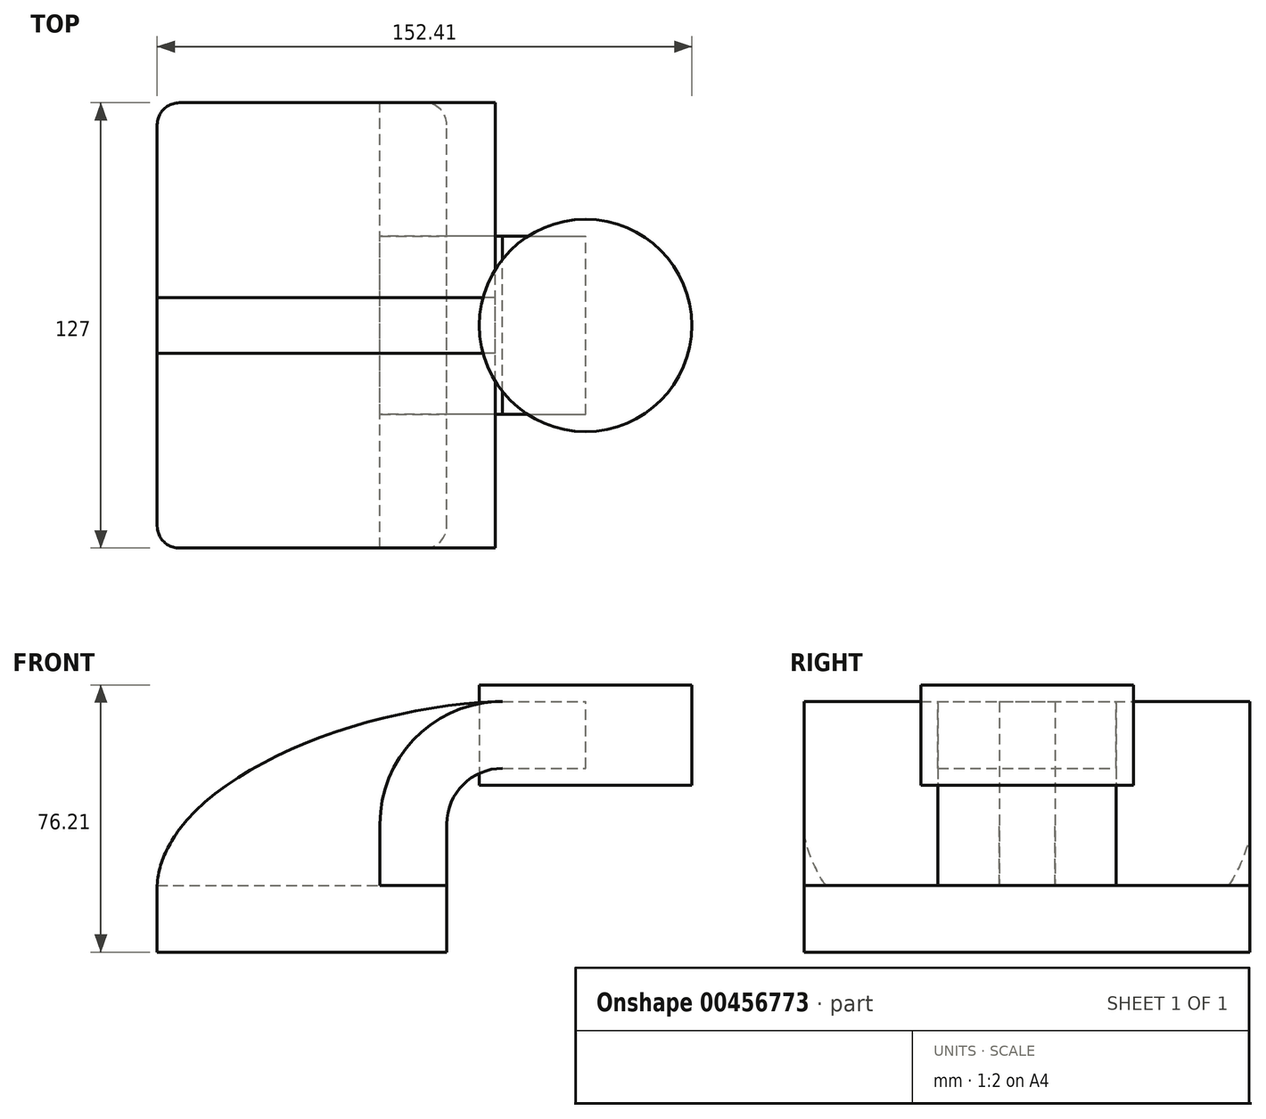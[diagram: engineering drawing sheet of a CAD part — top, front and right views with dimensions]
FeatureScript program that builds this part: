
annotation { "Feature Type Name" : "Feature", "Feature Type Description" : "" }
export const myFeature = defineFeature(function(context is Context, id is Id, definition is map)
    precondition{}
    {
        {
            var Q0;
            Q0=qCreatedBy(makeId("Front.planeOp"),FACE);
            var sketch = newSketch(context, id + "F0", { "sketchPlane" : qUnion([Q0])});
            skLineSegment(sketch, "E0.bottom", {"start": v(-41.28, -9.52) * mm, "end": v(41.28, -9.52) * mm});
            skLineSegment(sketch, "E0.top", {"start": v(-41.28, 9.53) * mm, "end": v(41.28, 9.53) * mm});
            skLineSegment(sketch, "E0.left", {"start": v(-41.27, -9.52) * mm, "end": v(-41.28, 9.53) * mm});
            skLineSegment(sketch, "E0.right", {"start": v(41.28, -9.52) * mm, "end": v(41.28, 9.53) * mm});
            skPoint(sketch, "E0.middle", {"position": v(0, 0) * mm});
            skLineSegment(sketch, "E1.bottom", {"start": v(60.32, 38.1) * mm, "end": v(111.12, 38.1) * mm});
            skLineSegment(sketch, "E1.top", {"start": v(60.32, 66.68) * mm, "end": v(111.12, 66.68) * mm});
            skLineSegment(sketch, "E1.left", {"start": v(60.32, 38.1) * mm, "end": v(60.32, 66.68) * mm});
            skLineSegment(sketch, "E1.right", {"start": v(111.12, 38.1) * mm, "end": v(111.12, 66.68) * mm});
            skPoint(sketch, "E1.middle", {"position": v(85.72, 52.39) * mm});
            skLineSegment(sketch, "E2", {"start": v(41.28, 9.53) * mm, "end": v(41.28, 27) * mm});
            skLineSegment(sketch, "E3", {"start": v(57.15, 42.88) * mm, "end": v(80.84, 42.88) * mm});
            skArc(sketch, "E4", {"start": v(41.27, 27) * mm, "mid": v(45.92, 38.23) * mm, "end": v(57.15, 42.88) * mm});
            skLineSegment(sketch, "E5.0", {"start": v(57.15, 61.93) * mm, "end": v(80.84, 61.93) * mm});
            skArc(sketch, "E5.1", {"start": v(22.22, 27) * mm, "mid": v(32.45, 51.7) * mm, "end": v(57.15, 61.93) * mm});
            skLineSegment(sketch, "E5.2", {"start": v(22.22, 9.53) * mm, "end": v(22.22, 27) * mm});
            skFitSpline(sketch, "E6", {"points": [v(57.15, 61.93) * mm, v(-41.27, 9.53) * mm], "startDerivative": vector(-127.55, -2.69) * mm, "endDerivative": vector(-5.26, -87.33) * mm});
            skLineSegment(sketch, "E7", {"start": v(80.84, 38.1) * mm, "end": v(80.84, 66.68) * mm});
            skSolve(sketch);
        }
        {
            var Q0;
            {var subQ0=sQuery(id+"F0.wireOp",EDGE,"E6");var subQ1=sQuery(id+"F0.wireOp",EDGE,"E5.1");var subQ3=makeQuery(id+"F0.imprint","INTERSECT",VERTEX,{"derivedFrom":[subQ1,subQ0]});Q0=makeQuery(id+"F0.imprint","IMPRINT",FACE,{"disambiguationData":[TD([[makeQuery(id+"F0.imprint","IMPRINT",EDGE,{"disambiguationData":[TD([[subQ3,-1.0]])],"derivedFrom":subQ1}),-1.0]])]});}
            var Q1;
            Q1=makeQuery(id+"F0.imprint","IMPRINT",FACE,{"disambiguationData":[TD([[makeQuery(id+"F0.imprint","IMPRINT",EDGE,{"derivedFrom":sQuery(id+"F0.wireOp",EDGE,"E0.bottom")}),1.0]])]});
            extrude(context, id + "F1", {"entities" : qUnion([Q0, Q1]), "endBound" : BoundingType.SYMMETRIC, "depth" : 127 * mm});
        }
        {
            var Q0;
            {var subQ4=sQuery(id+"F0.wireOp",EDGE,"E2");Q0=makeQuery(id+"F0.imprint","IMPRINT",FACE,{"disambiguationData":[TD([[makeQuery(id+"F0.imprint","IMPRINT",EDGE,{"derivedFrom":subQ4}),1.0]])]});}
            var Q1;
            {var subQ0=sQuery(id+"F0.wireOp",EDGE,"E3");var subQ1=sQuery(id+"F0.wireOp",EDGE,"E1.left");var subQ2=makeQuery(id+"F0.imprint","INTERSECT",VERTEX,{"derivedFrom":[subQ1,subQ0]});Q1=makeQuery(id+"F0.imprint","IMPRINT",FACE,{"disambiguationData":[TD([[makeQuery(id+"F0.imprint","IMPRINT",EDGE,{"disambiguationData":[TD([[subQ2,-1.0]])],"derivedFrom":subQ1}),-1.0]])]});}
            extrude(context, id + "F2", {"entities" : qUnion([Q0, Q1]), "endBound" : BoundingType.SYMMETRIC, "depth" : 50.8 * mm});
        }
        {
            var Q0;
            {var subQ3=sQuery(id+"F0.wireOp",EDGE,"E5.2");Q0=makeQuery(id+"F0.imprint","IMPRINT",FACE,{"disambiguationData":[TD([[makeQuery(id+"F0.imprint","IMPRINT",EDGE,{"derivedFrom":subQ3}),1.0]])]});}
            extrude(context, id + "F3", {"entities" : qUnion([Q0]), "endBound" : BoundingType.SYMMETRIC, "depth" : 15.88 * mm});
        }
        {
            var Q0;
            {var subQ4=sQuery(id+"F0.wireOp",EDGE,"E1.right");Q0=makeQuery(id+"F0.imprint","IMPRINT",FACE,{"disambiguationData":[TD([[makeQuery(id+"F0.imprint","IMPRINT",EDGE,{"derivedFrom":subQ4}),1.0]])]});}
            var Q1;
            Q1=sQuery(id+"F0.wireOp",EDGE,"E7");
            revolve(context, id + "F4", {"entities" : qUnion([Q0]), "axis" : qUnion([Q1]), "revolveType" : RevolveType.FULL});
        }
        {
            var Q0;
            Q0=makeQuery(id+"F1.opExtrude","CAP_EDGE",EDGE,{"disambiguationData":[OSD([sQuery(id+"F0.wireOp",EDGE,"E0.left")])],"isStart":false});
            var Q1;
            Q1=makeQuery(id+"F1.opExtrude","CAP_EDGE",EDGE,{"disambiguationData":[OSD([sQuery(id+"F0.wireOp",EDGE,"E0.right")])],"isStart":false});
            var Q2;
            Q2=makeQuery(id+"F1.opExtrude","CAP_EDGE",EDGE,{"disambiguationData":[OSD([sQuery(id+"F0.wireOp",EDGE,"E0.right")])],"isStart":true});
            var Q3;
            Q3=makeQuery(id+"F1.opExtrude","CAP_EDGE",EDGE,{"disambiguationData":[OSD([sQuery(id+"F0.wireOp",EDGE,"E0.left")])],"isStart":true});
            fillet(context, id + "F5", {"entities" : qUnion([Q0, Q1, Q2, Q3]), "radius" : 6.35 * mm, "tangentPropagation" : true, "allowEdgeOverflow" : false});
        }
    });
